# Revit family: Калитка WHD-15
name_source: partatom
category: Обобщенные модели
units: mm (PartAtom-declared; Revit-internal decimal feet)

## family parameters
Всегда вертикально = Да
Может служить основой для арматурных стержней = Нет
На основе рабочей плоскости = Нет
Общий = Нет
При загрузке вырезать с полостями = Нет
Размер круглого соединителя = Использовать диаметр
Тип детали = Нормальный
Точка расчета площади = Нет

## types (1)
- Калитка WHD-15
    ADSK_URL страницы изделия = https://www.perco.ru
    ADSK_Единица измерения = компл.
    ADSK_Завод-изготовитель = PERCo
    ADSK_Количество = 1
    ADSK_Масса_Текст = 35 кг
    ADSK_Материал наименование = Сталь окрашенная RAL 1019
    ADSK_Напряжение = от 11,5 до 14 В постоянного тока
    ADSK_Номинальная мощность = 36 Вт
    ADSK_Ток = 3 А
    Габаритные размеры = 2150х1232х378,5 мм
    Отметка по умолчанию = 0 мм
    Подключение к электросети = 220 В
    Пропускная способность = 12 чел./мин
    Степень защиты оболочки = IP54
    Температура использования = от -30°C до +50°C
    Ширина зоны прохода = Ширина зоны прохода
